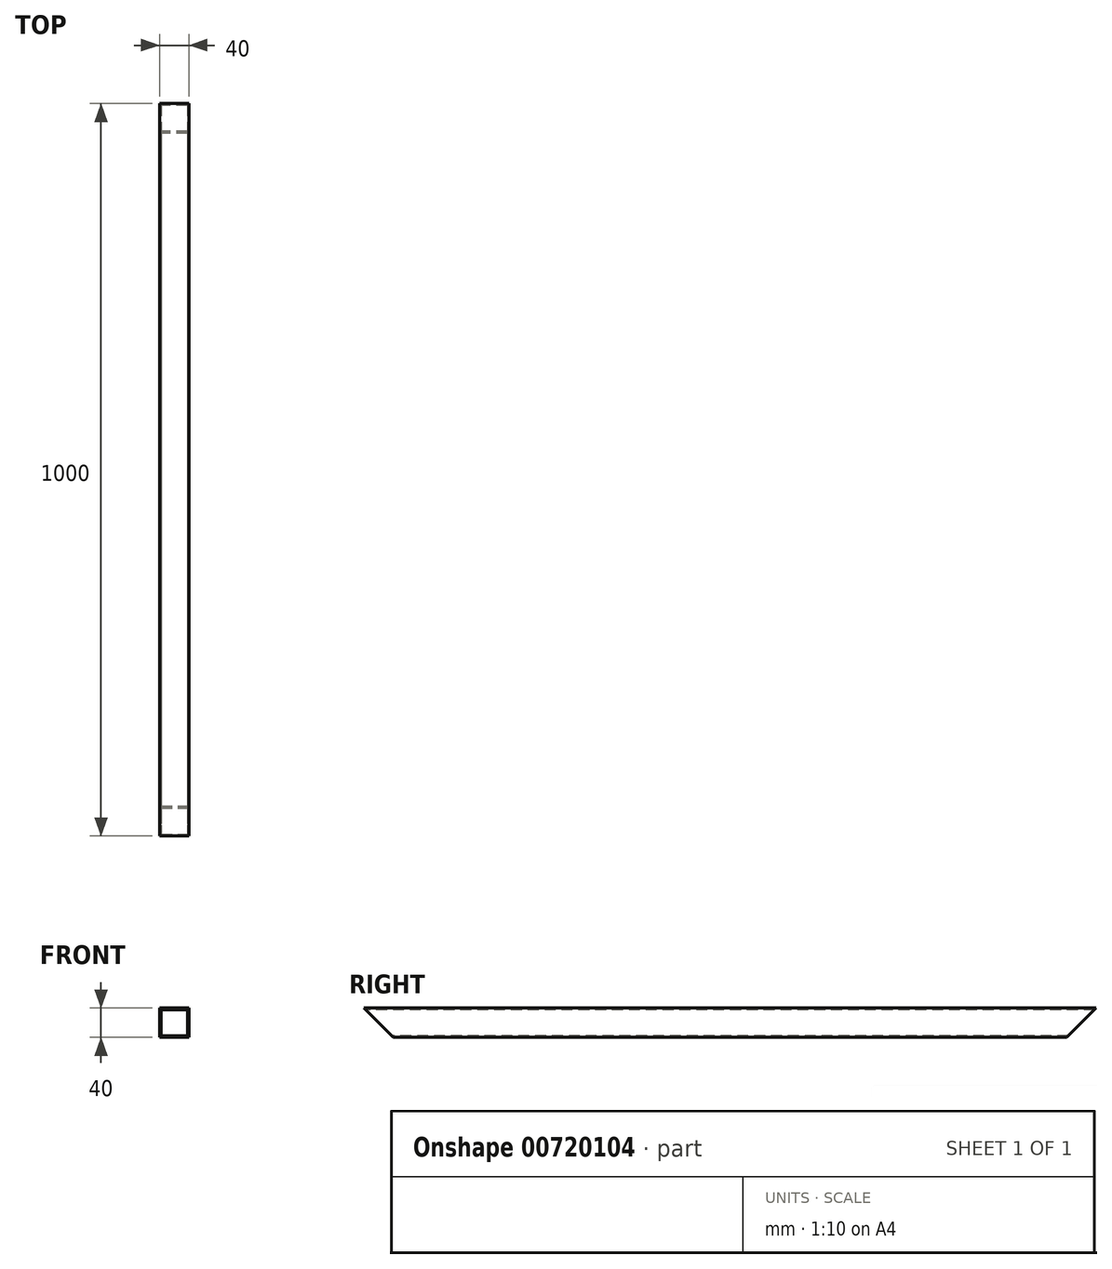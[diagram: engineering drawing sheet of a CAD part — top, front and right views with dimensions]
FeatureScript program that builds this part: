
annotation { "Feature Type Name" : "Feature", "Feature Type Description" : "" }
export const myFeature = defineFeature(function(context is Context, id is Id, definition is map)
    precondition{}
    {
        {
            var Q0;
            Q0=qCreatedBy(makeId("Front.planeOp"),FACE);
            var sketch = newSketch(context, id + "F0", { "sketchPlane" : qUnion([Q0])});
            skLineSegment(sketch, "E0.bottom", {"start": v(0, 0) * mm, "end": v(40, 0) * mm});
            skLineSegment(sketch, "E0.top", {"start": v(0, 40) * mm, "end": v(40, 40) * mm});
            skLineSegment(sketch, "E0.left", {"start": v(0, 0) * mm, "end": v(0, 40) * mm});
            skLineSegment(sketch, "E0.right", {"start": v(40, 0) * mm, "end": v(40, 40) * mm});
            skSolve(sketch);
        }
        {
            var Q0;
            Q0 = qSketchRegion(id + "F0", true);
            extrude(context, id + "F1", {"entities" : qUnion([Q0]), "depth" : 1000 * mm, "offsetDistance" : 25 * mm});
        }
        {
            var Q0;
            Q0=makeQuery(id+"F1.opExtrude","CAP_FACE",FACE,{"disambiguationData":[OSD([sQuery(id+"F0.wireOp",EDGE,"E0.bottom"),sQuery(id+"F0.wireOp",EDGE,"E0.top"),sQuery(id+"F0.wireOp",EDGE,"E0.left"),sQuery(id+"F0.wireOp",EDGE,"E0.right")])],"isStart":false});
            var sketch = newSketch(context, id + "F2", { "sketchPlane" : qUnion([Q0])});
            skLineSegment(sketch, "E1.bottom", {"start": v(2, 2) * mm, "end": v(38, 2) * mm});
            skLineSegment(sketch, "E1.top", {"start": v(2, 38) * mm, "end": v(38, 38) * mm});
            skLineSegment(sketch, "E1.left", {"start": v(2, 2) * mm, "end": v(2, 38) * mm});
            skLineSegment(sketch, "E1.right", {"start": v(38, 2) * mm, "end": v(38, 38) * mm});
            skSolve(sketch);
        }
        {
            var Q0;
            Q0=makeQuery(id+"F2.imprint","IMPRINT",FACE,{"disambiguationData":[TD([[makeQuery(id+"F2.imprint","IMPRINT",EDGE,{"derivedFrom":sQuery(id+"F2.wireOp",EDGE,"E1.bottom")}),1.0]])]});
            extrude(context, id + "F3", {"entities" : qUnion([Q0]), "operationType" : NewBodyOperationType.REMOVE, "endBound" : BoundingType.THROUGH_ALL, "oppositeDirection" : true, "depth" : 25 * mm, "offsetDistance" : 25 * mm});
        }
        {
            var Q0;
            Q0=makeQuery(id+"F1.opExtrude","CAP_EDGE",EDGE,{"disambiguationData":[OSD([sQuery(id+"F0.wireOp",EDGE,"E0.bottom")])],"isStart":false});
            var Q1;
            Q1=makeQuery(id+"F1.opExtrude","CAP_EDGE",EDGE,{"disambiguationData":[OSD([sQuery(id+"F0.wireOp",EDGE,"E0.bottom")])],"isStart":true});
            chamfer(context, id + "F4", {"entities" : qUnion([Q0, Q1]), "width" : 40 * mm, "tangentPropagation" : true});
        }
    });
